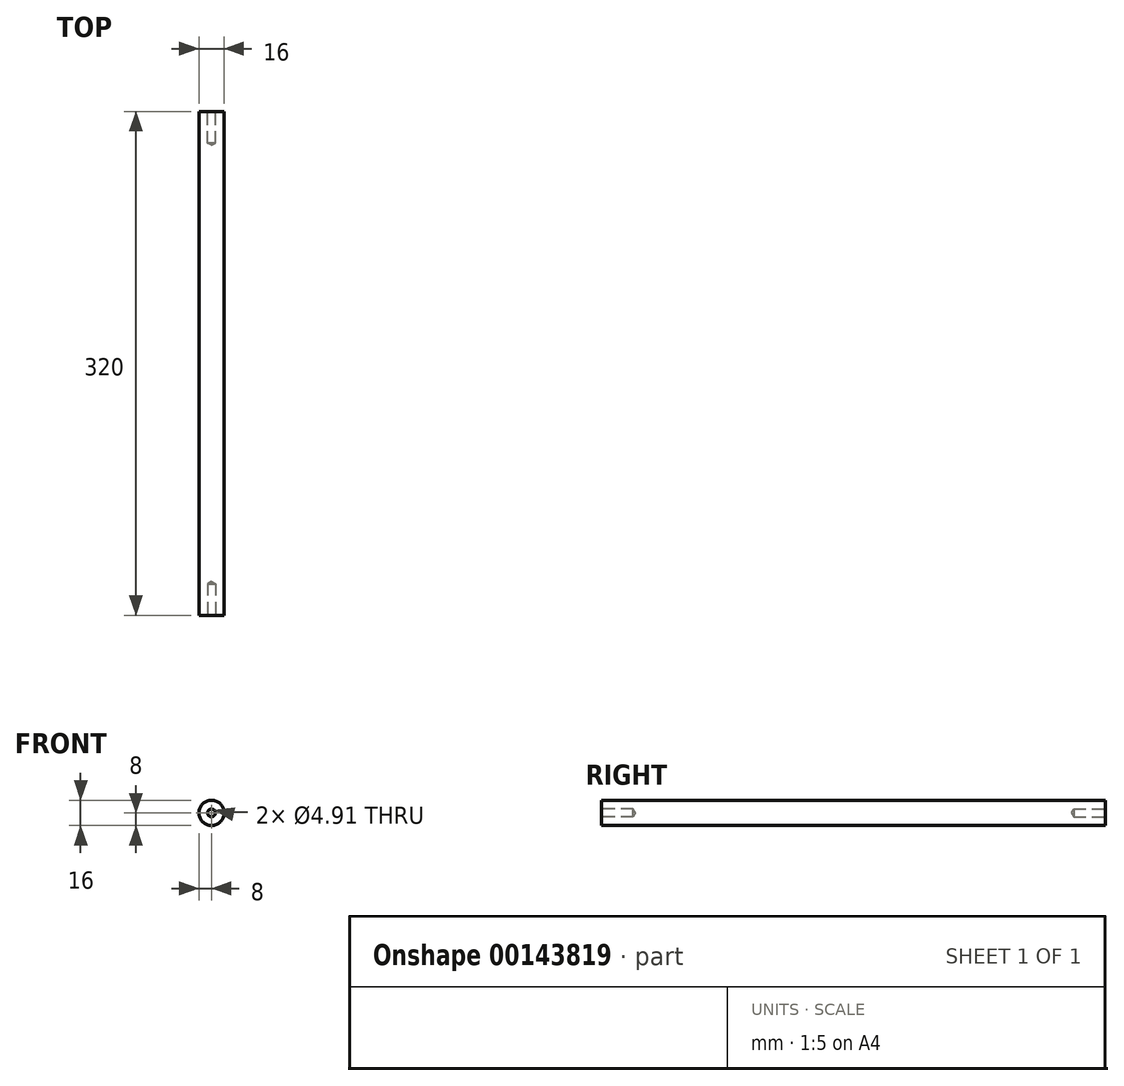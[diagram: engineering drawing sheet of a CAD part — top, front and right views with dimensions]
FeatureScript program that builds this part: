
annotation { "Feature Type Name" : "Feature", "Feature Type Description" : "" }
export const myFeature = defineFeature(function(context is Context, id is Id, definition is map)
    precondition{}
    {
        {
            var Q0;
            Q0=qCreatedBy(makeId("Front.planeOp"),FACE);
            var sketch = newSketch(context, id + "F0", { "sketchPlane" : qUnion([Q0])});
            skCircle(sketch, "E0", {"center": v(0, 0) * mm, "radius": 8 * mm});
            skCircle(sketch, "E1", {"center": v(0, 0) * mm, "radius": 2.46 * mm});
            skSolve(sketch);
        }
        {
            var Q0;
            Q0=makeQuery(id+"F0.imprint","IMPRINT",FACE,{"disambiguationData":[TD([[makeQuery(id+"F0.imprint","IMPRINT",EDGE,{"derivedFrom":sQuery(id+"F0.wireOp",EDGE,"E0")}),1.0]])]});
            var Q1;
            Q1=makeQuery(id+"F0.imprint","IMPRINT",FACE,{"disambiguationData":[TD([[makeQuery(id+"F0.imprint","IMPRINT",EDGE,{"derivedFrom":sQuery(id+"F0.wireOp",EDGE,"E1")}),1.0]])]});
            extrude(context, id + "F1", {"entities" : qUnion([Q0, Q1]), "depth" : 320 * mm});
        }
        {
            var Q0;
            Q0=makeQuery(id+"F1.opExtrude","CAP_FACE",FACE,{"disambiguationData":[OSD([sQuery(id+"F0.wireOp",EDGE,"E0")])],"isStart":true});
            var sketch = newSketch(context, id + "F2", { "sketchPlane" : qUnion([Q0])});
            skCircle(sketch, "E2", {"center": v(0, 0) * mm, "radius": 2.46 * mm});
            skSolve(sketch);
        }
        {
            var Q0;
            Q0=makeQuery(id+"F1.opExtrude","CAP_FACE",FACE,{"disambiguationData":[OSD([sQuery(id+"F0.wireOp",EDGE,"E0")])],"isStart":false});
            var sketch = newSketch(context, id + "F3", { "sketchPlane" : qUnion([Q0])});
            skCircle(sketch, "E3", {"center": v(0, 0) * mm, "radius": 2.46 * mm});
            skSolve(sketch);
        }
        {
            var Q0;
            Q0=sQuery(id+"F3.wireOp",VERTEX,"E3.center");
            var Q1;
            Q1=makeQuery(id+"F1.opExtrude","SWEPT_BODY",BODY,{"disambiguationData":[OSD([sQuery(id+"F0.wireOp",EDGE,"E0")])]});
            hole(context, id + "F4", {"style" : HoleStyle.SIMPLE, "endStyle" : HoleEndStyle.BLIND, "holeDiameter" : 4.9 * mm, "holeDepth" : 20 * mm, "startFromSketch" : true, "locations" : qUnion([Q0]), "scope" : qUnion([Q1])});
        }
        {
            var Q0;
            Q0=sQuery(id+"F2.wireOp",VERTEX,"E2.center");
            var Q1;
            Q1=makeQuery(id+"F1.opExtrude","SWEPT_BODY",BODY,{"disambiguationData":[OSD([sQuery(id+"F0.wireOp",EDGE,"E0")])]});
            hole(context, id + "F5", {"style" : HoleStyle.SIMPLE, "endStyle" : HoleEndStyle.BLIND, "holeDiameter" : 4.9 * mm, "holeDepth" : 20 * mm, "startFromSketch" : true, "locations" : qUnion([Q0]), "scope" : qUnion([Q1])});
        }
    });
